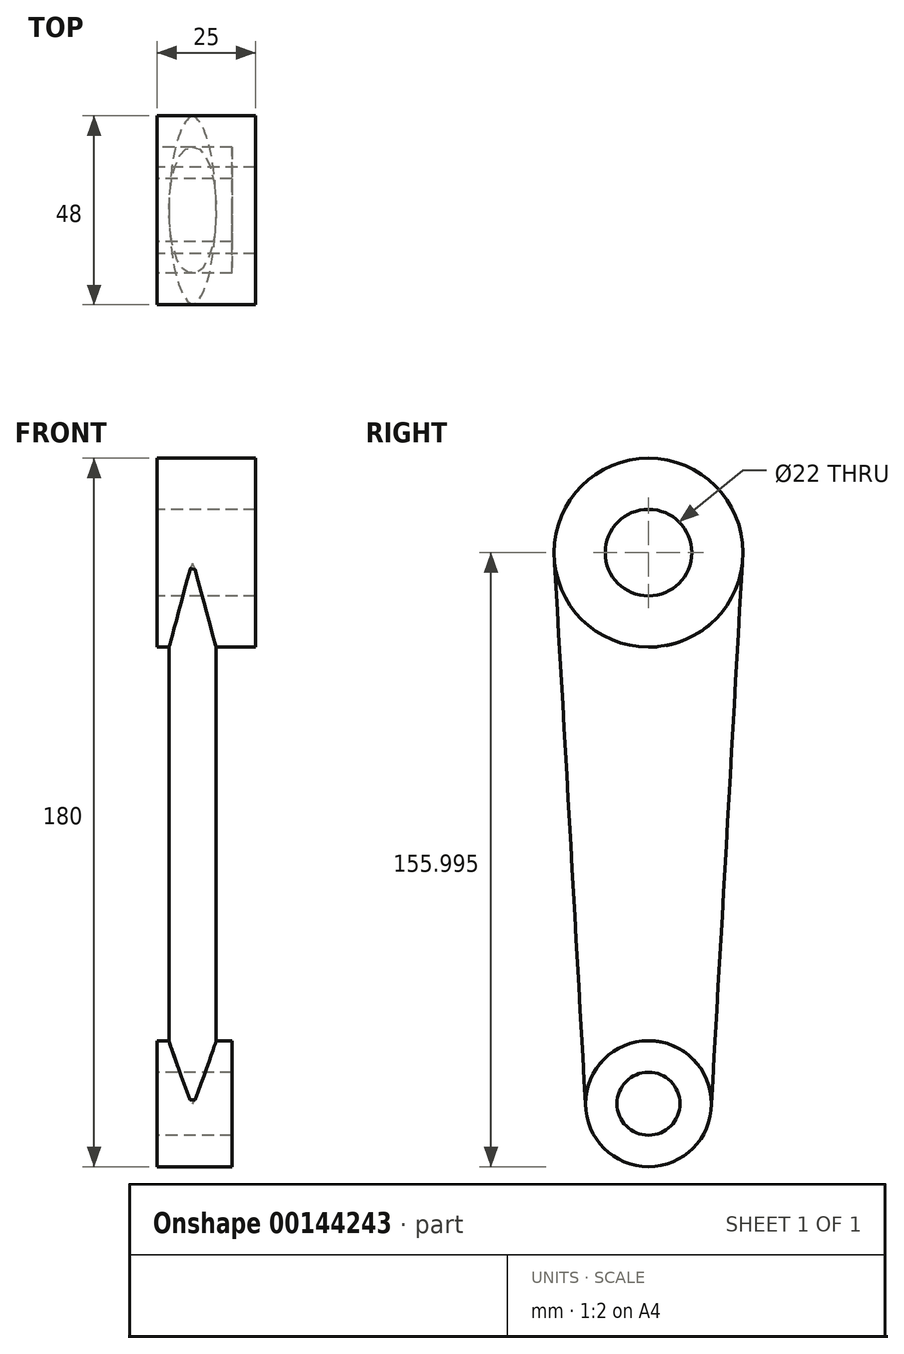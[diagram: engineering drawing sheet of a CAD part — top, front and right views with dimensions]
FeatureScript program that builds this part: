
annotation { "Feature Type Name" : "Feature", "Feature Type Description" : "" }
export const myFeature = defineFeature(function(context is Context, id is Id, definition is map)
    precondition{}
    {
        {
            var Q0;
            Q0=qCreatedBy(makeId("Right.planeOp"),FACE);
            var sketch = newSketch(context, id + "F0", { "sketchPlane" : qUnion([Q0])});
            skLineSegment(sketch, "E0", {"start": v(0, 60.5) * mm, "end": v(0, -79.5) * mm, "construction": true});
            skCircle(sketch, "E1", {"center": v(0, 60.5) * mm, "radius": 24 * mm});
            skCircle(sketch, "E2", {"center": v(0, -79.5) * mm, "radius": 16 * mm});
            skCircle(sketch, "E3", {"center": v(0, 60.5) * mm, "radius": 11 * mm});
            skCircle(sketch, "E4", {"center": v(0, -79.5) * mm, "radius": 8 * mm});
            skLineSegment(sketch, "E5", {"start": v(-31.82, 60.5) * mm, "end": v(33.1, 60.5) * mm, "construction": true});
            skLineSegment(sketch, "E6", {"start": v(-25.04, -79.5) * mm, "end": v(39, -79.5) * mm, "construction": true});
            skSolve(sketch);
        }
        {
            var Q0;
            Q0=makeQuery(id+"F0.imprint","IMPRINT",FACE,{"disambiguationData":[TD([[makeQuery(id+"F0.imprint","IMPRINT",EDGE,{"derivedFrom":sQuery(id+"F0.wireOp",EDGE,"E2")}),1.0]])]});
            extrude(context, id + "F1", {"entities" : qUnion([Q0]), "depth" : 19 * mm});
        }
        {
            var Q0;
            Q0=sQuery(id+"F0.wireOp",VERTEX,"E3.center");
            var Q1;
            Q1=qCreatedBy(makeId("Top.planeOp"),FACE);
            cPlane(context, id + "F2", {"entities" : qUnion([Q0, Q1]), "cplaneType" : CPlaneType.PLANE_POINT, "offset" : 25 * mm, "width" : 150 * mm, "height" : 150 * mm});
        }
        {
            var Q0;
            Q0=sQuery(id+"F0.wireOp",VERTEX,"E4.center");
            var Q1;
            Q1=qCreatedBy(makeId("Top.planeOp"),FACE);
            cPlane(context, id + "F3", {"entities" : qUnion([Q0, Q1]), "cplaneType" : CPlaneType.PLANE_POINT, "offset" : 25 * mm, "width" : 150 * mm, "height" : 150 * mm});
        }
        {
            var Q0;
            Q0=makeQuery(id+"F0.imprint","IMPRINT",FACE,{"disambiguationData":[TD([[makeQuery(id+"F0.imprint","IMPRINT",EDGE,{"derivedFrom":sQuery(id+"F0.wireOp",EDGE,"E1")}),1.0]])]});
            extrude(context, id + "F4", {"entities" : qUnion([Q0]), "depth" : 25 * mm});
        }
        {
            var Q0;
            Q0=qCreatedBy(id+"F3.planeOp",FACE);
            var sketch = newSketch(context, id + "F5", { "sketchPlane" : qUnion([Q0])});
            skEllipse(sketch, "E7", {"center": v(9, 0) * mm, "majorRadius": 16 * mm, "minorRadius": 6 * mm, "majorAxis": v(0, 1)});
            skPoint(sketch, "E8", {"position": v(3, 0) * mm});
            skLineSegment(sketch, "E9.0", {"start": v(0, 8) * mm, "end": v(0, -8) * mm});
            skLineSegment(sketch, "E10", {"start": v(0, 16) * mm, "end": v(19, 16) * mm, "construction": true});
            skSolve(sketch);
        }
        {
            var Q0;
            Q0=qCreatedBy(id+"F2.planeOp",FACE);
            var sketch = newSketch(context, id + "F6", { "sketchPlane" : qUnion([Q0])});
            skEllipse(sketch, "E11", {"center": v(9, 0) * mm, "majorRadius": 24 * mm, "minorRadius": 6 * mm, "majorAxis": v(0, 1)});
            skPoint(sketch, "E12", {"position": v(3, 0) * mm});
            skLineSegment(sketch, "E13", {"start": v(0, 24) * mm, "end": v(25, 24) * mm, "construction": true});
            skSolve(sketch);
        }
        {
            var Q0;
            Q0=makeQuery(id+"F6.imprint","IMPRINT",FACE,{"disambiguationData":[TD([[makeQuery(id+"F6.imprint","IMPRINT",EDGE,{"derivedFrom":sQuery(id+"F6.wireOp",EDGE,"E11")}),1.0]])]});
            var Q1;
            Q1=makeQuery(id+"F5.imprint","IMPRINT",FACE,{"disambiguationData":[TD([[makeQuery(id+"F5.imprint","IMPRINT",EDGE,{"derivedFrom":sQuery(id+"F5.wireOp",EDGE,"E7")}),1.0]])]});
            loft(context, id + "F7", {"operationType" : NewBodyOperationType.ADD, "sheetProfilesArray" : [{ "sheetProfileEntities" : qUnion([Q0]) }, { "sheetProfileEntities" : qUnion([Q1]) }]});
        }
        {
            var Q0;
            Q0=makeQuery(id+"F0.imprint","IMPRINT",FACE,{"disambiguationData":[TD([[makeQuery(id+"F0.imprint","IMPRINT",EDGE,{"derivedFrom":sQuery(id+"F0.wireOp",EDGE,"E4")}),1.0]])]});
            var Q1;
            Q1=makeQuery(id+"F0.imprint","IMPRINT",FACE,{"disambiguationData":[TD([[makeQuery(id+"F0.imprint","IMPRINT",EDGE,{"derivedFrom":sQuery(id+"F0.wireOp",EDGE,"E3")}),1.0]])]});
            extrude(context, id + "F8", {"entities" : qUnion([Q0, Q1]), "operationType" : NewBodyOperationType.REMOVE, "depth" : 25 * mm});
        }
    });
